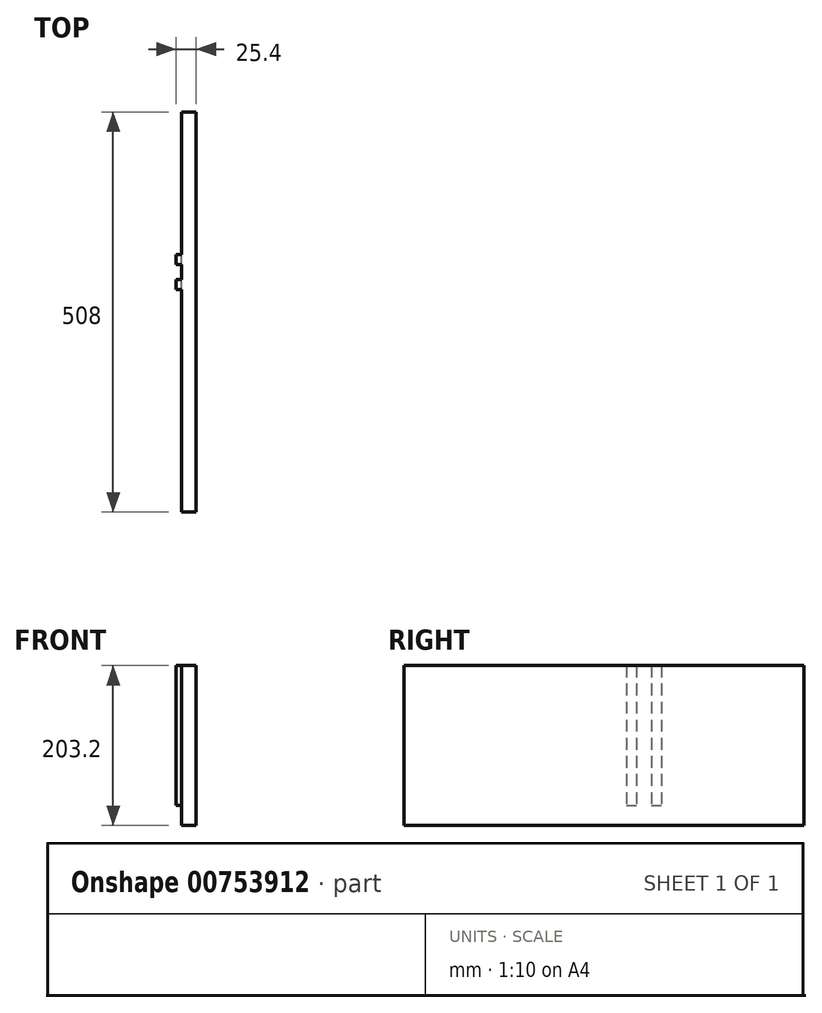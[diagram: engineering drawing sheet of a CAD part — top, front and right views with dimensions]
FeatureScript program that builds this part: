
annotation { "Feature Type Name" : "Feature", "Feature Type Description" : "" }
export const myFeature = defineFeature(function(context is Context, id is Id, definition is map)
    precondition{}
    {
        {
            var Q0;
            Q0=qCreatedBy(makeId("Right.planeOp"),FACE);
            var sketch = newSketch(context, id + "F0", { "sketchPlane" : qUnion([Q0])});
            skLineSegment(sketch, "E0.bottom", {"start": v(254, -101.6) * mm, "end": v(-254, -101.6) * mm});
            skLineSegment(sketch, "E0.top", {"start": v(254, 101.6) * mm, "end": v(-254, 101.6) * mm});
            skLineSegment(sketch, "E0.left", {"start": v(254, -101.6) * mm, "end": v(254, 101.6) * mm});
            skLineSegment(sketch, "E0.right", {"start": v(-254, -101.6) * mm, "end": v(-254, 101.6) * mm});
            skPoint(sketch, "E0.middle", {"position": v(0, 0) * mm});
            skSolve(sketch);
        }
        {
            var Q0;
            Q0=makeQuery(id+"F0.imprint","IMPRINT",FACE,{"disambiguationData":[TD([[makeQuery(id+"F0.imprint","IMPRINT",EDGE,{"derivedFrom":sQuery(id+"F0.wireOp",EDGE,"E0.bottom")}),-1.0]])]});
            extrude(context, id + "F1", {"entities" : qUnion([Q0]), "depth" : 19.05 * mm, "offsetDistance" : 25.4 * mm});
        }
        {
            var Q0;
            Q0=makeQuery(id+"F1.opExtrude","CAP_FACE",FACE,{"disambiguationData":[OSD([sQuery(id+"F0.wireOp",EDGE,"E0.bottom"),sQuery(id+"F0.wireOp",EDGE,"E0.top"),sQuery(id+"F0.wireOp",EDGE,"E0.left"),sQuery(id+"F0.wireOp",EDGE,"E0.right")])],"isStart":true});
            var sketch = newSketch(context, id + "F2", { "sketchPlane" : qUnion([Q0])});
            skLineSegment(sketch, "E1", {"start": v(0, 0) * mm, "end": v(-254, 0) * mm});
            skLineSegment(sketch, "E2.bottom", {"start": v(-28.58, 101.6) * mm, "end": v(-73.03, 101.6) * mm});
            skLineSegment(sketch, "E2.top", {"start": v(-28.58, -101.6) * mm, "end": v(-73.03, -101.6) * mm});
            skLineSegment(sketch, "E2.left", {"start": v(-28.58, 101.6) * mm, "end": v(-28.58, -101.6) * mm});
            skLineSegment(sketch, "E2.right", {"start": v(-73.03, 101.6) * mm, "end": v(-73.03, -101.6) * mm});
            skPoint(sketch, "E2.middle", {"position": v(-50.8, 0) * mm});
            skLineSegment(sketch, "E3.0", {"start": v(-60.33, 101.6) * mm, "end": v(-60.33, -101.6) * mm});
            skLineSegment(sketch, "E4.0", {"start": v(-41.28, 101.6) * mm, "end": v(-41.28, -101.6) * mm});
            skLineSegment(sketch, "E5", {"start": v(-254, 0) * mm, "end": v(-50.8, 0) * mm});
            skLineSegment(sketch, "E6.0", {"start": v(-28.58, -76.2) * mm, "end": v(-73.03, -76.2) * mm});
            skLineSegment(sketch, "E7", {"start": v(-60.33, -101.6) * mm, "end": v(-41.28, -101.6) * mm});
            skSolve(sketch);
        }
        {
            var Q0;
            {var subQ1=sQuery(id+"F2.wireOp",EDGE,"E2.bottom");var subQ3=sQuery(id+"F2.wireOp",EDGE,"E3.0");var subQ4=makeQuery(id+"F2.imprint","INTERSECT",VERTEX,{"derivedFrom":[subQ1,subQ3]});Q0=makeQuery(id+"F2.imprint","IMPRINT",FACE,{"disambiguationData":[TD([[makeQuery(id+"F2.imprint","IMPRINT",EDGE,{"disambiguationData":[TD([[subQ4,-1.0]])],"derivedFrom":subQ3}),-1.0]])]});}
            var Q1;
            {var subQ0=sQuery(id+"F2.wireOp",EDGE,"E6.0");var subQ1=sQuery(id+"F2.wireOp",EDGE,"E2.right");var subQ2=makeQuery(id+"F2.imprint","INTERSECT",VERTEX,{"derivedFrom":[subQ1,subQ0]});Q1=makeQuery(id+"F2.imprint","IMPRINT",FACE,{"disambiguationData":[TD([[makeQuery(id+"F2.imprint","IMPRINT",EDGE,{"disambiguationData":[TD([[subQ2,1.0]])],"derivedFrom":subQ1}),1.0]])]});}
            var Q2;
            {var subQ0=sQuery(id+"F2.wireOp",EDGE,"E2.left");var subQ1=sQuery(id+"F2.wireOp",EDGE,"E1");var subQ2=makeQuery(id+"F2.imprint","INTERSECT",VERTEX,{"derivedFrom":[subQ1,subQ0]});Q2=makeQuery(id+"F2.imprint","IMPRINT",FACE,{"disambiguationData":[TD([[makeQuery(id+"F2.imprint","IMPRINT",EDGE,{"disambiguationData":[TD([[subQ2,-1.0]])],"derivedFrom":subQ1}),1.0]])]});}
            var Q3;
            {var subQ0=sQuery(id+"F2.wireOp",EDGE,"E2.left");var subQ1=sQuery(id+"F2.wireOp",EDGE,"E1");var subQ2=makeQuery(id+"F2.imprint","INTERSECT",VERTEX,{"derivedFrom":[subQ1,subQ0]});Q3=makeQuery(id+"F2.imprint","IMPRINT",FACE,{"disambiguationData":[TD([[makeQuery(id+"F2.imprint","IMPRINT",EDGE,{"disambiguationData":[TD([[subQ2,-1.0]])],"derivedFrom":subQ1}),-1.0]])]});}
            extrude(context, id + "F3", {"entities" : qUnion([Q0, Q1, Q2, Q3]), "operationType" : NewBodyOperationType.ADD, "depth" : 6.35 * mm, "offsetDistance" : 25.4 * mm});
        }
    });
